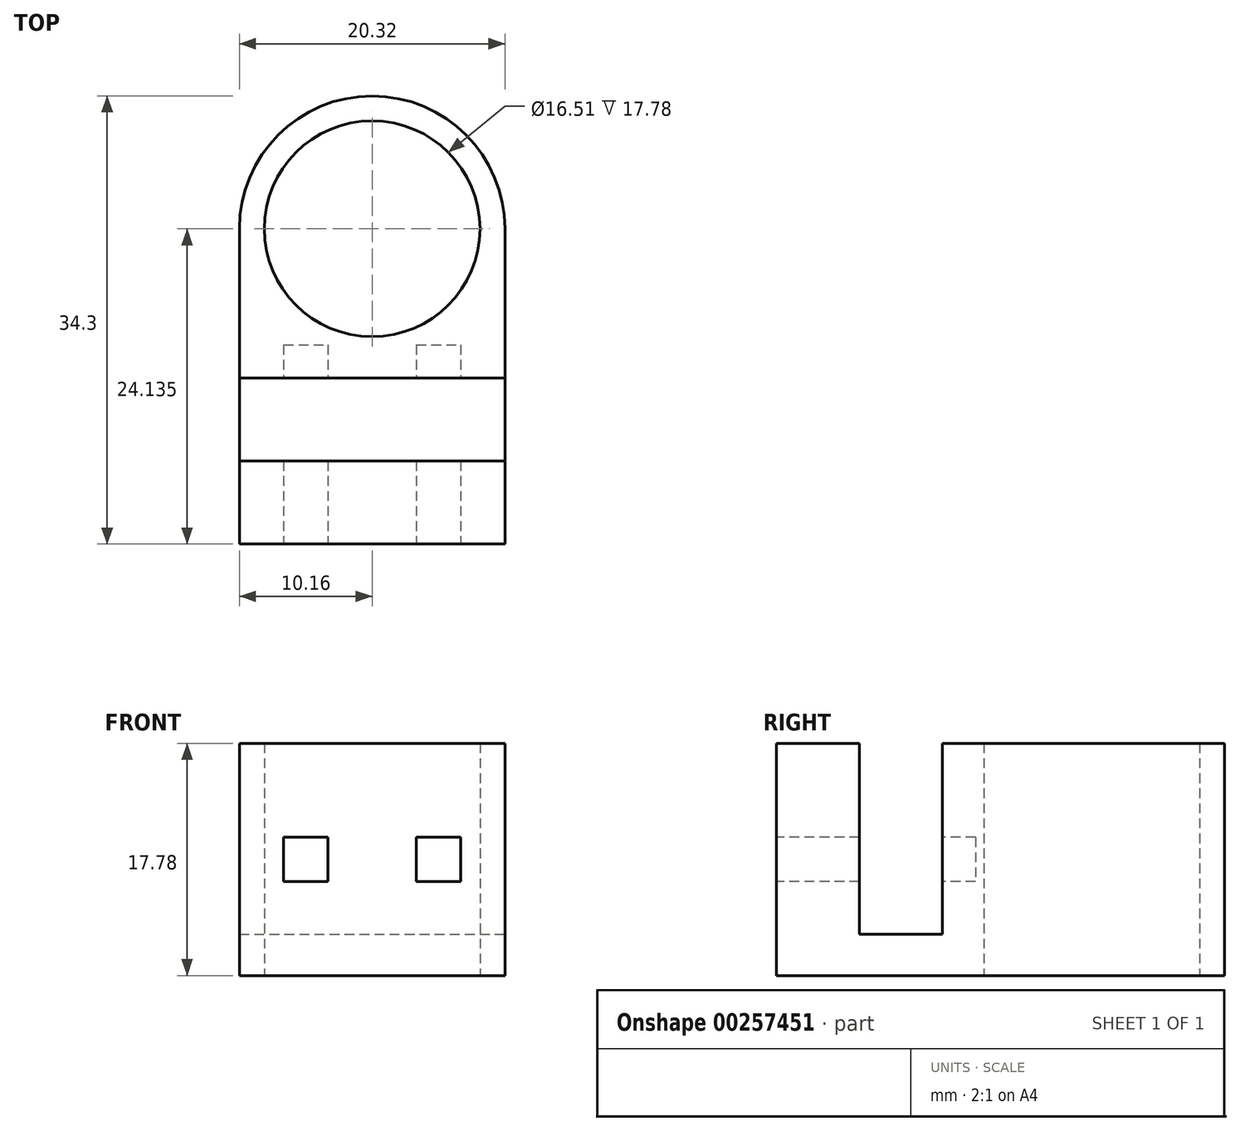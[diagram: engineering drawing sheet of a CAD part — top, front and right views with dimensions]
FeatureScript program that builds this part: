
annotation { "Feature Type Name" : "Feature", "Feature Type Description" : "" }
export const myFeature = defineFeature(function(context is Context, id is Id, definition is map)
    precondition{}
    {
        {
            var Q0;
            Q0=qCreatedBy(makeId("Top.planeOp"),FACE);
            var sketch = newSketch(context, id + "F0", { "sketchPlane" : qUnion([Q0])});
            skLineSegment(sketch, "E0.bottom", {"start": v(10.16, -6.35) * mm, "end": v(-10.16, -6.35) * mm});
            skLineSegment(sketch, "E0.top", {"start": v(10.16, 6.35) * mm, "end": v(-10.16, 6.35) * mm});
            skLineSegment(sketch, "E0.left", {"start": v(10.16, -6.35) * mm, "end": v(10.16, 6.35) * mm});
            skLineSegment(sketch, "E0.right", {"start": v(-10.16, -6.35) * mm, "end": v(-10.16, 6.35) * mm});
            skPoint(sketch, "E0.middle", {"position": v(0, 0) * mm});
            skSolve(sketch);
        }
        {
            var Q0;
            Q0 = qSketchRegion(id + "F0", true);
            extrude(context, id + "F1", {"entities" : qUnion([Q0]), "depth" : 3.17 * mm});
        }
        {
            var Q0;
            Q0=makeQuery(id+"F1.opExtrude","CAP_FACE",FACE,{"disambiguationData":[OSD([sQuery(id+"F0.wireOp",EDGE,"E0.bottom"),sQuery(id+"F0.wireOp",EDGE,"E0.top"),sQuery(id+"F0.wireOp",EDGE,"E0.left"),sQuery(id+"F0.wireOp",EDGE,"E0.right")])],"isStart":false});
            var sketch = newSketch(context, id + "F2", { "sketchPlane" : qUnion([Q0])});
            skLineSegment(sketch, "E1.bottom", {"start": v(-10.16, 6.35) * mm, "end": v(10.16, 6.35) * mm});
            skLineSegment(sketch, "E1.top", {"start": v(-10.16, 3.18) * mm, "end": v(10.16, 3.18) * mm});
            skLineSegment(sketch, "E1.left", {"start": v(-10.16, 6.35) * mm, "end": v(-10.16, 3.18) * mm});
            skLineSegment(sketch, "E1.right", {"start": v(10.16, 6.35) * mm, "end": v(10.16, 3.18) * mm});
            skLineSegment(sketch, "E2.bottom", {"start": v(-10.16, -6.35) * mm, "end": v(10.16, -6.35) * mm});
            skLineSegment(sketch, "E2.top", {"start": v(-10.16, -3.18) * mm, "end": v(10.16, -3.18) * mm});
            skLineSegment(sketch, "E2.left", {"start": v(-10.16, -6.35) * mm, "end": v(-10.16, -3.18) * mm});
            skLineSegment(sketch, "E2.right", {"start": v(10.16, -6.35) * mm, "end": v(10.16, -3.18) * mm});
            skSolve(sketch);
        }
        {
            var Q0;
            Q0=makeQuery(id+"F2.imprint","IMPRINT",FACE,{"disambiguationData":[TD([[makeQuery(id+"F2.imprint","IMPRINT",EDGE,{"derivedFrom":sQuery(id+"F2.wireOp",EDGE,"E2.bottom")}),-1.0]])]});
            extrude(context, id + "F3", {"entities" : qUnion([Q0]), "operationType" : NewBodyOperationType.ADD, "depth" : 14.6 * mm});
        }
        {
            var Q0;
            Q0=qCreatedBy(makeId("Top.planeOp"),FACE);
            var sketch = newSketch(context, id + "F4", { "sketchPlane" : qUnion([Q0])});
            skCircle(sketch, "E3", {"center": v(0, 14.6) * mm, "radius": 8.26 * mm});
            skArc(sketch, "E4", {"start": v(10.16, 14.6) * mm, "mid": v(0, 24.77) * mm, "end": v(-10.16, 14.6) * mm});
            skLineSegment(sketch, "E5", {"start": v(10.16, 14.6) * mm, "end": v(10.16, 3.18) * mm});
            skLineSegment(sketch, "E6", {"start": v(-10.16, 14.6) * mm, "end": v(-10.16, 3.18) * mm});
            skLineSegment(sketch, "E7", {"start": v(-10.16, 3.18) * mm, "end": v(10.16, 3.18) * mm});
            skSolve(sketch);
        }
        {
            var Q0;
            Q0=makeQuery(id+"F4.imprint","IMPRINT",FACE,{"disambiguationData":[TD([[makeQuery(id+"F4.imprint","IMPRINT",EDGE,{"derivedFrom":sQuery(id+"F4.wireOp",EDGE,"E3")}),-1.0]])]});
            extrude(context, id + "F5", {"entities" : qUnion([Q0]), "operationType" : NewBodyOperationType.ADD, "depth" : 17.78 * mm});
        }
        {
            var Q0;
            Q0=makeQuery(id+"F3.boolean.opBoolean","MERGE",FACE,{"derivedFrom":[makeQuery(id+"F1.opExtrude","SWEPT_FACE",FACE,{"disambiguationData":[OSD([sQuery(id+"F0.wireOp",EDGE,"E0.bottom")])]}),makeQuery(id+"F3.opExtrude","SWEPT_FACE",FACE,{"disambiguationData":[OSD([sQuery(id+"F2.wireOp",EDGE,"E2.bottom")])]})]});
            var sketch = newSketch(context, id + "F6", { "sketchPlane" : qUnion([Q0])});
            skLineSegment(sketch, "E8.bottom", {"start": v(-10.16, 17.78) * mm, "end": v(10.16, 17.78) * mm});
            skLineSegment(sketch, "E8.top", {"start": v(-10.16, 0) * mm, "end": v(10.16, 0) * mm});
            skLineSegment(sketch, "E8.left", {"start": v(-10.16, 17.78) * mm, "end": v(-10.16, 0) * mm});
            skLineSegment(sketch, "E8.right", {"start": v(10.16, 17.78) * mm, "end": v(10.16, 0) * mm});
            skSolve(sketch);
        }
        {
            var Q0;
            Q0 = qSketchRegion(id + "F6", true);
            extrude(context, id + "F7", {"entities" : qUnion([Q0]), "operationType" : NewBodyOperationType.ADD, "depth" : 3.17 * mm});
        }
        {
            var Q0;
            Q0=makeQuery(id+"F7.opExtrude","CAP_FACE",FACE,{"disambiguationData":[OSD([sQuery(id+"F6.wireOp",EDGE,"E8.bottom"),sQuery(id+"F6.wireOp",EDGE,"E8.top"),sQuery(id+"F6.wireOp",EDGE,"E8.left"),sQuery(id+"F6.wireOp",EDGE,"E8.right")])],"isStart":false});
            var sketch = newSketch(context, id + "F8", { "sketchPlane" : qUnion([Q0])});
            skLineSegment(sketch, "E9.bottom", {"start": v(-6.77, 10.58) * mm, "end": v(-3.39, 10.58) * mm});
            skLineSegment(sketch, "E9.top", {"start": v(-6.77, 7.2) * mm, "end": v(-3.39, 7.2) * mm});
            skLineSegment(sketch, "E9.left", {"start": v(-6.77, 10.58) * mm, "end": v(-6.77, 7.2) * mm});
            skLineSegment(sketch, "E9.right", {"start": v(-3.39, 10.58) * mm, "end": v(-3.39, 7.2) * mm});
            skLineSegment(sketch, "E10.bottom", {"start": v(3.39, 10.58) * mm, "end": v(6.77, 10.58) * mm});
            skLineSegment(sketch, "E10.top", {"start": v(3.39, 7.2) * mm, "end": v(6.77, 7.2) * mm});
            skLineSegment(sketch, "E10.left", {"start": v(3.39, 10.58) * mm, "end": v(3.39, 7.2) * mm});
            skLineSegment(sketch, "E10.right", {"start": v(6.77, 10.58) * mm, "end": v(6.77, 7.2) * mm});
            skSolve(sketch);
        }
        {
            var Q0;
            Q0 = qSketchRegion(id + "F8", true);
            extrude(context, id + "F9", {"entities" : qUnion([Q0]), "operationType" : NewBodyOperationType.REMOVE, "oppositeDirection" : true, "depth" : 15.24 * mm});
        }
    });
